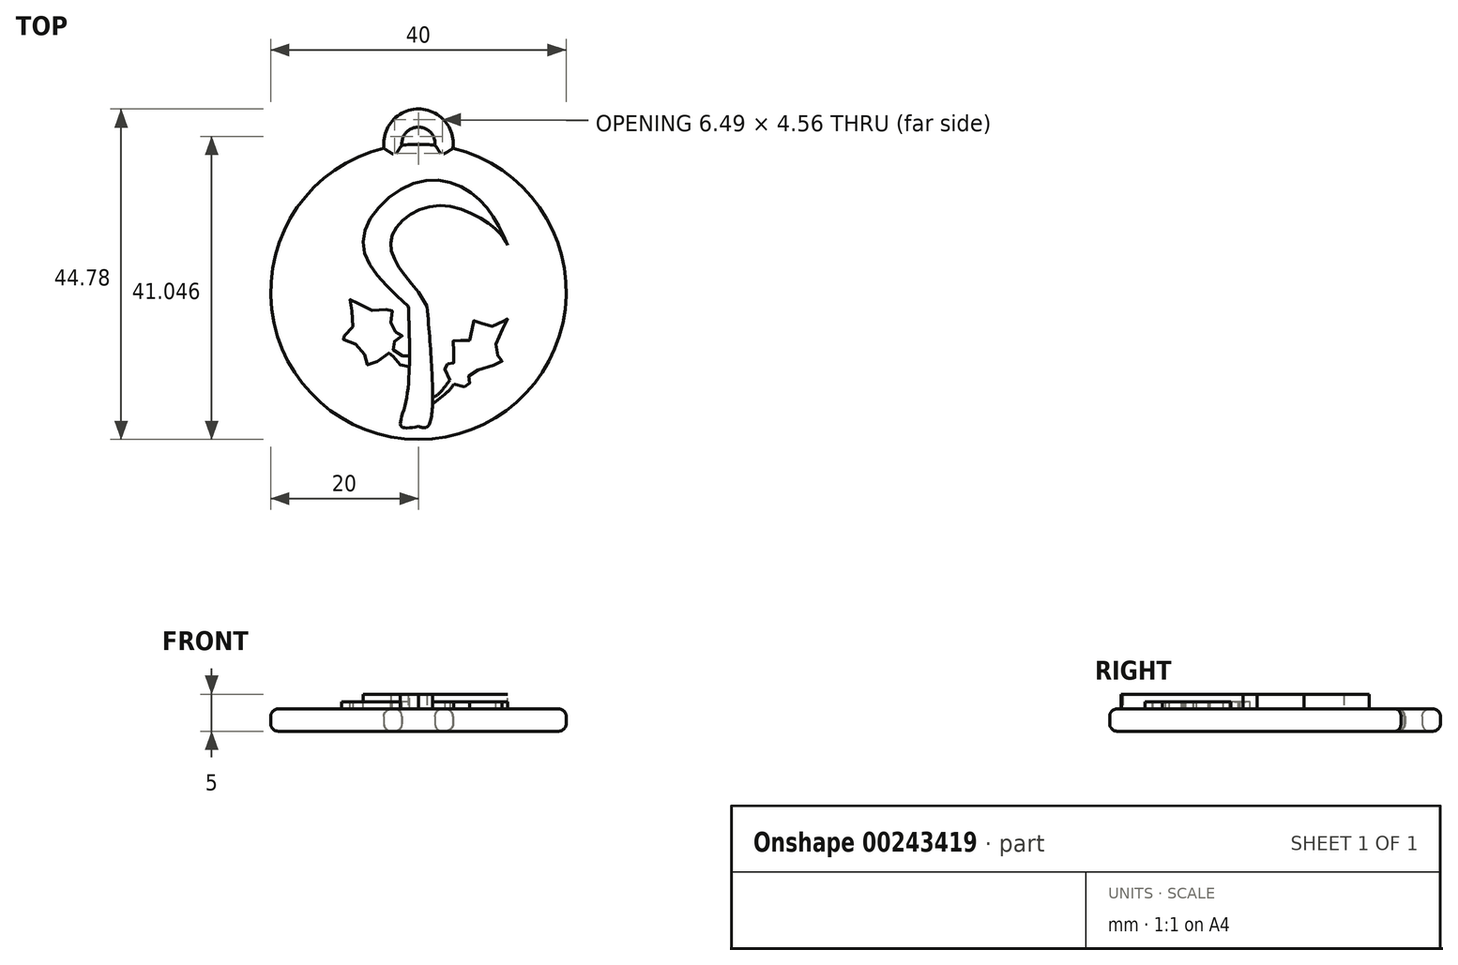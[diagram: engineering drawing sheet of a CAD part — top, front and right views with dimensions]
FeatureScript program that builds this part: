
annotation { "Feature Type Name" : "Feature", "Feature Type Description" : "" }
export const myFeature = defineFeature(function(context is Context, id is Id, definition is map)
    precondition{}
    {
        {
            var Q0;
            Q0=qCreatedBy(makeId("Top.planeOp"),FACE);
            var sketch = newSketch(context, id + "F0", { "sketchPlane" : qUnion([Q0])});
            skCircle(sketch, "E0", {"center": v(0, 0) * mm, "radius": 20 * mm});
            skSolve(sketch);
        }
        {
            var Q0;
            Q0=makeQuery(id+"F0.imprint","IMPRINT",FACE,{"disambiguationData":[TD([[makeQuery(id+"F0.imprint","IMPRINT",EDGE,{"derivedFrom":sQuery(id+"F0.wireOp",EDGE,"E0")}),1.0]])]});
            extrude(context, id + "F1", {"entities" : qUnion([Q0]), "depth" : 3 * mm});
        }
        {
            var Q0;
            Q0=makeQuery(id+"F1.opExtrude","CAP_FACE",FACE,{"disambiguationData":[OSD([sQuery(id+"F0.wireOp",EDGE,"E0")])],"isStart":false});
            var sketch = newSketch(context, id + "F2", { "sketchPlane" : qUnion([Q0])});
            skLineSegment(sketch, "E1", {"start": v(0, -18.22) * mm, "end": v(0, 0) * mm});
            skFitSpline(sketch, "E2", {"points": [v(0, 0) * mm, v(-3.7, 7.1) * mm, v(2.63, 11.69) * mm, v(10.81, 8.18) * mm, v(12.08, 6.33) * mm], "startDerivative": vector(-22.15, 25.74) * mm, "endDerivative": vector(5.23, -11.28) * mm});
            skFitSpline(sketch, "E3", {"points": [v(0, -18.22) * mm, v(-2.34, -18.22) * mm, v(-1.75, -15.1) * mm, v(-1.36, -1.95) * mm], "startDerivative": vector(-13.79, -2.42) * mm, "endDerivative": vector(-1, 28.57) * mm});
            skFitSpline(sketch, "E4", {"points": [v(0, -18.22) * mm, v(1.27, -18.22) * mm, v(1.17, -1.95) * mm], "startDerivative": vector(6.45, -2.27) * mm, "endDerivative": vector(-2.44, 28.94) * mm});
            skFitSpline(sketch, "E5", {"points": [v(-1.36, -1.95) * mm, v(-7.5, 7.1) * mm, v(0, 14.9) * mm, v(8.18, 12.56) * mm, v(12.08, 6.33) * mm], "startDerivative": vector(-35.5, 32.1) * mm, "endDerivative": vector(13.66, -30.39) * mm});
            skFitSpline(sketch, "E6", {"points": [v(1.17, -1.95) * mm, v(0, 0) * mm], "startDerivative": vector(-1.17, 1.95) * mm, "endDerivative": vector(-1.17, 1.95) * mm});
            skFitSpline(sketch, "E7", {"points": [v(1.9, -15.2) * mm, v(4.77, -12.47) * mm, v(4.77, -11.2) * mm], "startDerivative": vector(5.75, 4.56) * mm, "endDerivative": vector(0.08, 3.53) * mm});
            skFitSpline(sketch, "E8", {"points": [v(4.77, -12.47) * mm, v(6.91, -12.47) * mm, v(6.91, -11.2) * mm, v(11.3, -9.45) * mm, v(10.42, -7.99) * mm, v(12.08, -3.6) * mm, v(9.74, -4.68) * mm, v(7.5, -3.9) * mm, v(6.82, -6.63) * mm, v(4.77, -6.53) * mm, v(4.77, -9.65) * mm, v(3.7, -9.84) * mm, v(4.77, -12.47) * mm]});
            skFitSpline(sketch, "E9", {"points": [v(4.77, -11.2) * mm, v(1.9, -14.23) * mm, v(0.78, -12.47) * mm], "startDerivative": vector(-5.54, -7.91) * mm, "endDerivative": vector(-2.26, 6.18) * mm});
            skFitSpline(sketch, "E10", {"points": [v(-1.23, -10.13) * mm, v(-3.6, -8.67) * mm, v(-3.8, -7.9) * mm], "startDerivative": vector(-4.6, 2.26) * mm, "endDerivative": vector(-0.02, 2.22) * mm});
            skFitSpline(sketch, "E11", {"points": [v(-1.21, -8.67) * mm, v(-2.23, -8.67) * mm, v(-3.6, -7.02) * mm], "startDerivative": vector(-2.54, -0.57) * mm, "endDerivative": vector(-2.26, 3.63) * mm});
            skFitSpline(sketch, "E12", {"points": [v(-3.6, -7.02) * mm, v(-2.24, -5.94) * mm, v(-3.6, -4.97) * mm, v(-3.6, -2.44) * mm, v(-6.24, -2.53) * mm, v(-9.16, -1.07) * mm, v(-8.96, -4.87) * mm, v(-10.42, -6.24) * mm, v(-7.7, -7.73) * mm, v(-6.72, -9.94) * mm, v(-3.8, -8.15) * mm], "startDerivative": vector(28.23, 15.38) * mm, "endDerivative": vector(40.71, 32.82) * mm});
            skSolve(sketch);
        }
        {
            var Q0;
            Q0=makeQuery(id+"F2.imprint","IMPRINT",FACE,{"disambiguationData":[TD([[makeQuery(id+"F2.imprint","IMPRINT",EDGE,{"derivedFrom":sQuery(id+"F2.wireOp",EDGE,"E2")}),-1.0]])]});
            var sketch = newSketch(context, id + "F3", { "sketchPlane" : qUnion([Q0])});
            skFitSpline(sketch, "E13", {"points": [v(-3.8, -8.13) * mm, v(-3.57, -7.23) * mm, v(-3.57, -7) * mm, v(-3.8, -8.13) * mm]});
            skSolve(sketch);
        }
        {
            var Q0;
            Q0=makeQuery(id+"F2.imprint","IMPRINT",FACE,{"disambiguationData":[TD([[makeQuery(id+"F2.imprint","IMPRINT",EDGE,{"derivedFrom":sQuery(id+"F2.wireOp",EDGE,"E2")}),-1.0]])]});
            var sketch = newSketch(context, id + "F4", { "sketchPlane" : qUnion([Q0])});
            skFitSpline(sketch, "E14", {"points": [v(-1.25, -10.13) * mm, v(-3.22, -9.2) * mm, v(-3.8, -8.2) * mm, v(-6.72, -9.97) * mm, v(-7.7, -7.71) * mm, v(-10.4, -6.27) * mm, v(-8.95, -4.88) * mm, v(-9.24, -1.02) * mm, v(-6.18, -2.53) * mm, v(-3.57, -2.4) * mm, v(-3.6, -5.01) * mm, v(-2.19, -5.91) * mm, v(-3.6, -7.1) * mm, v(-2.12, -8.68) * mm, v(-1.22, -8.68) * mm, v(-1.25, -10.13) * mm]});
            skSolve(sketch);
        }
        {
            var Q0;
            {var subQ0=sQuery(id+"F4.wireOp",EDGE,"E14");var subQ1=sQuery(id+"F2.wireOp",EDGE,"E3");var subQ2=makeQuery(id+"F2.imprint","IMPRINT",EDGE,{"disambiguationData":[TD([[makeQuery(id+"F2.imprint","IMPRINT",VERTEX,{"disambiguationData":[OD(0.0)],"derivedFrom":subQ1}),-1.0]])],"derivedFrom":subQ1});var subQ3=makeQuery(id+"F4.imprint","INTERSECT",VERTEX,{"disambiguationData":[OD(0.0)],"derivedFrom":[subQ2,subQ0]});Q0=makeQuery(id+"F4.imprint","IMPRINT",FACE,{"disambiguationData":[TD([[makeQuery(id+"F4.imprint","IMPRINT",EDGE,{"disambiguationData":[TD([[subQ3,-1.0]])],"derivedFrom":subQ0}),-1.0]])]});}
            extrude(context, id + "F5", {"entities" : qUnion([Q0]), "operationType" : NewBodyOperationType.ADD, "depth" : 1 * mm});
        }
        {
            var Q0;
            {var subQ4=sQuery(id+"F2.wireOp",EDGE,"E1");Q0=makeQuery(id+"F2.imprint","IMPRINT",FACE,{"disambiguationData":[TD([[makeQuery(id+"F2.imprint","IMPRINT",EDGE,{"derivedFrom":subQ4}),-1.0]])]});}
            var Q1;
            {var subQ3=sQuery(id+"F2.wireOp",EDGE,"E1");Q1=makeQuery(id+"F2.imprint","IMPRINT",FACE,{"disambiguationData":[TD([[makeQuery(id+"F2.imprint","IMPRINT",EDGE,{"derivedFrom":subQ3}),1.0]])]});}
            extrude(context, id + "F6", {"entities" : qUnion([Q0, Q1]), "operationType" : NewBodyOperationType.ADD, "depth" : 2 * mm});
        }
        {
            var Q0;
            Q0=makeQuery(id+"F3.imprint","IMPRINT",FACE,{"disambiguationData":[TD([[makeQuery(id+"F3.imprint","IMPRINT",EDGE,{"derivedFrom":makeQuery(id+"F2.imprint","IMPRINT",EDGE,{"derivedFrom":sQuery(id+"F2.wireOp",EDGE,"E2")})}),1.0]])]});
            extrude(context, id + "F7", {"entities" : qUnion([Q0]), "operationType" : NewBodyOperationType.ADD, "depth" : 1 * mm});
        }
        {
            var Q0;
            Q0=qCreatedBy(makeId("Top.planeOp"),FACE);
            var sketch = newSketch(context, id + "F8", { "sketchPlane" : qUnion([Q0])});
            skCircle(sketch, "E15", {"center": v(0, 20.07) * mm, "radius": 2.26 * mm});
            skCircle(sketch, "E16", {"center": v(0, 20.07) * mm, "radius": 4.71 * mm});
            skSolve(sketch);
        }
        {
            var Q0;
            Q0=makeQuery(id+"F8.imprint","IMPRINT",FACE,{"disambiguationData":[TD([[makeQuery(id+"F8.imprint","IMPRINT",EDGE,{"derivedFrom":sQuery(id+"F8.wireOp",EDGE,"E15")}),-1.0]])]});
            extrude(context, id + "F9", {"entities" : qUnion([Q0]), "operationType" : NewBodyOperationType.ADD, "depth" : 3 * mm});
        }
        {
            var Q0;
            Q0=makeQuery(id+"F9.opExtrude","CAP_EDGE",EDGE,{"disambiguationData":[OSD([sQuery(id+"F8.wireOp",EDGE,"E16")])],"isStart":false});
            var Q1;
            {var subQ0=sQuery(id+"F0.wireOp",EDGE,"E0");var subQ1=sQuery(id+"F8.wireOp",EDGE,"E16");Q1=makeQuery(id+"F9.boolean.opBoolean","SPLIT",EDGE,{"disambiguationData":[TD([makeQuery(id+"F9.opExtrude","SWEPT_FACE",FACE,{"disambiguationData":[OSD([subQ1])]})])],"derivedFrom":makeQuery(id+"F1.opExtrude","CAP_EDGE",EDGE,{"disambiguationData":[OSD([subQ0])],"isStart":true})});}
            var Q2;
            Q2=makeQuery(id+"F9.opExtrude","CAP_EDGE",EDGE,{"disambiguationData":[OSD([sQuery(id+"F8.wireOp",EDGE,"E16")])],"isStart":true});
            var Q3;
            {var subQ0=sQuery(id+"F0.wireOp",EDGE,"E0");var subQ1=sQuery(id+"F8.wireOp",EDGE,"E16");Q3=makeQuery(id+"F9.boolean.opBoolean","SPLIT",EDGE,{"disambiguationData":[TD([makeQuery(id+"F9.opExtrude","SWEPT_FACE",FACE,{"disambiguationData":[OSD([subQ1])]})])],"derivedFrom":makeQuery(id+"F1.opExtrude","CAP_EDGE",EDGE,{"disambiguationData":[OSD([subQ0])],"isStart":false})});}
            var Q4;
            {var subQ0=sQuery(id+"F0.wireOp",EDGE,"E0");var subQ1=sQuery(id+"F8.wireOp",EDGE,"E15");Q4=makeQuery(id+"F9.boolean.opBoolean","SPLIT",EDGE,{"disambiguationData":[TD([makeQuery(id+"F9.opExtrude","SWEPT_FACE",FACE,{"disambiguationData":[OSD([subQ1])]})])],"derivedFrom":makeQuery(id+"F1.opExtrude","CAP_EDGE",EDGE,{"disambiguationData":[OSD([subQ0])],"isStart":false})});}
            var Q5;
            {var subQ0=sQuery(id+"F0.wireOp",EDGE,"E0");var subQ1=sQuery(id+"F8.wireOp",EDGE,"E15");Q5=makeQuery(id+"F9.boolean.opBoolean","SPLIT",EDGE,{"disambiguationData":[TD([makeQuery(id+"F9.opExtrude","SWEPT_FACE",FACE,{"disambiguationData":[OSD([subQ1])]})])],"derivedFrom":makeQuery(id+"F1.opExtrude","CAP_EDGE",EDGE,{"disambiguationData":[OSD([subQ0])],"isStart":true})});}
            fillet(context, id + "F10", {"entities" : qUnion([Q0, Q1, Q2, Q3, Q4, Q5]), "radius" : 1 * mm, "tangentPropagation" : true, "allowEdgeOverflow" : false});
        }
        {
            var Q0;
            Q0=makeQuery(id+"F9.opExtrude","CAP_EDGE",EDGE,{"disambiguationData":[OSD([sQuery(id+"F8.wireOp",EDGE,"E15")])],"isStart":false});
            var Q1;
            Q1=makeQuery(id+"F9.opExtrude","CAP_EDGE",EDGE,{"disambiguationData":[OSD([sQuery(id+"F8.wireOp",EDGE,"E15")])],"isStart":true});
            fillet(context, id + "F11", {"entities" : qUnion([Q0, Q1]), "radius" : 1 * mm, "tangentPropagation" : true, "allowEdgeOverflow" : false});
        }
    });
